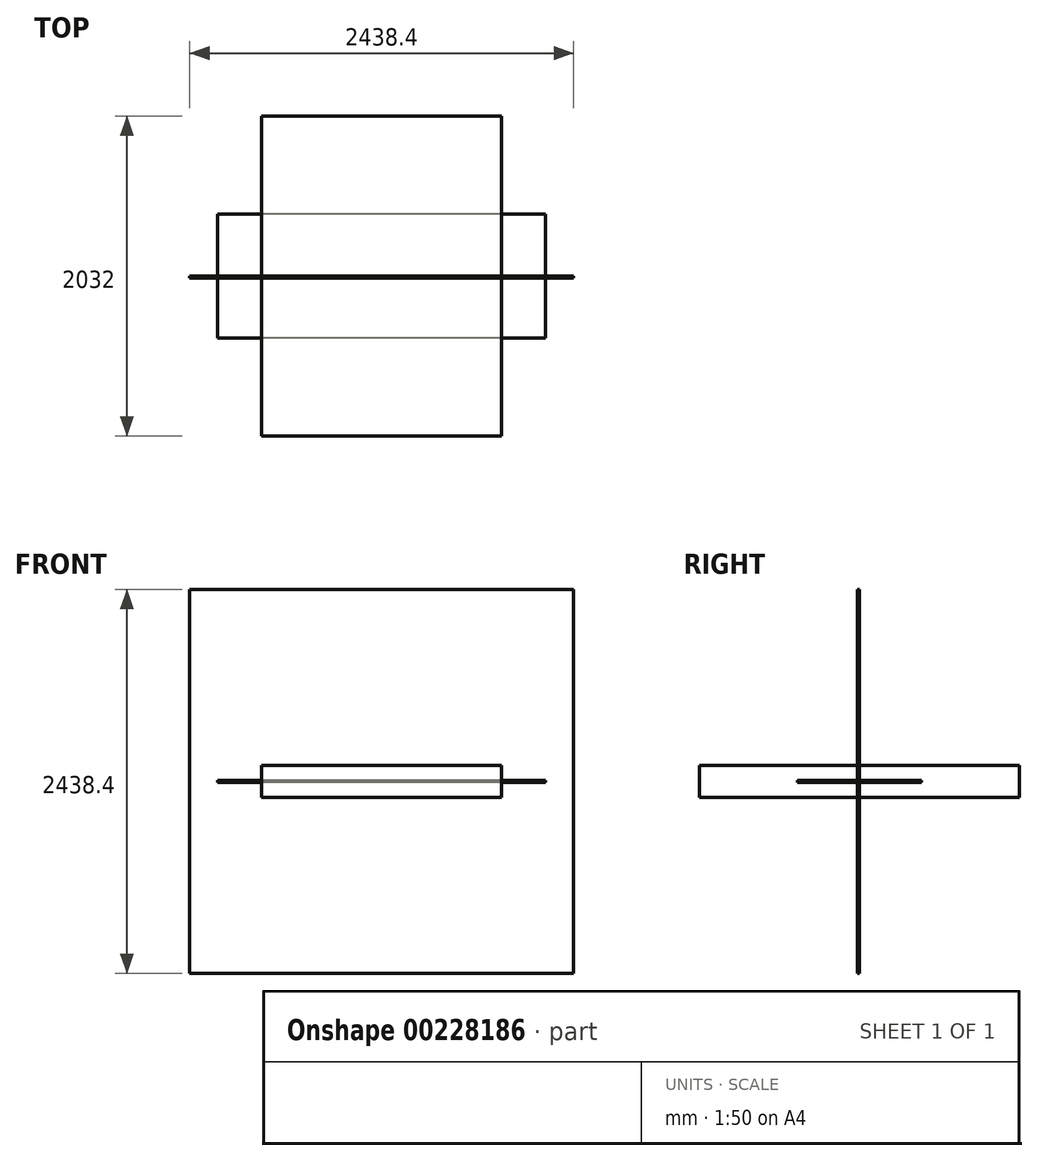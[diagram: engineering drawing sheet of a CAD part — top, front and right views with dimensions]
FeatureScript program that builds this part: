
annotation { "Feature Type Name" : "Feature", "Feature Type Description" : "" }
export const myFeature = defineFeature(function(context is Context, id is Id, definition is map)
    precondition{}
    {
        {
            var Q0;
            Q0=qCreatedBy(makeId("Top.planeOp"),FACE);
            var sketch = newSketch(context, id + "F0", { "sketchPlane" : qUnion([Q0])});
            skLineSegment(sketch, "E0.bottom", {"start": v(1041.4, 393.7) * mm, "end": v(-1041.4, 393.7) * mm});
            skLineSegment(sketch, "E0.top", {"start": v(1041.4, -393.7) * mm, "end": v(-1041.4, -393.7) * mm});
            skLineSegment(sketch, "E0.left", {"start": v(1041.4, 393.7) * mm, "end": v(1041.4, -393.7) * mm});
            skLineSegment(sketch, "E0.right", {"start": v(-1041.4, 393.7) * mm, "end": v(-1041.4, -393.7) * mm});
            skPoint(sketch, "E0.middle", {"position": v(0, 0) * mm});
            skSolve(sketch);
        }
        {
            var Q0;
            Q0=makeQuery(id+"F0.imprint","IMPRINT",FACE,{"disambiguationData":[TD([[makeQuery(id+"F0.imprint","IMPRINT",EDGE,{"derivedFrom":sQuery(id+"F0.wireOp",EDGE,"E0.bottom")}),1.0]])]});
            extrude(context, id + "F1", {"entities" : qUnion([Q0]), "endBound" : BoundingType.SYMMETRIC, "depth" : 11.9 * mm});
        }
        {
            var Q0;
            Q0=qCreatedBy(makeId("Top.planeOp"),FACE);
            var sketch = newSketch(context, id + "F2", { "sketchPlane" : qUnion([Q0])});
            skLineSegment(sketch, "E1.bottom", {"start": v(-762, 1016) * mm, "end": v(762, 1016) * mm});
            skLineSegment(sketch, "E1.top", {"start": v(-762, -1016) * mm, "end": v(762, -1016) * mm});
            skLineSegment(sketch, "E1.left", {"start": v(-762, 1016) * mm, "end": v(-762, -1016) * mm});
            skLineSegment(sketch, "E1.right", {"start": v(762, 1016) * mm, "end": v(762, -1016) * mm});
            skPoint(sketch, "E1.middle", {"position": v(0, 0) * mm});
            skSolve(sketch);
        }
        {
            var Q0;
            Q0 = qSketchRegion(id + "F2", true);
            extrude(context, id + "F3", {"entities" : qUnion([Q0]), "endBound" : BoundingType.SYMMETRIC, "depth" : 203.2 * mm});
        }
        {
            var Q0;
            Q0=qCreatedBy(makeId("Front.planeOp"),FACE);
            var sketch = newSketch(context, id + "F4", { "sketchPlane" : qUnion([Q0])});
            skLineSegment(sketch, "E2.bottom", {"start": v(1219.2, 1219.2) * mm, "end": v(-1219.2, 1219.2) * mm});
            skLineSegment(sketch, "E2.top", {"start": v(1219.2, -1219.2) * mm, "end": v(-1219.2, -1219.2) * mm});
            skLineSegment(sketch, "E2.left", {"start": v(1219.2, 1219.2) * mm, "end": v(1219.2, -1219.2) * mm});
            skLineSegment(sketch, "E2.right", {"start": v(-1219.2, 1219.2) * mm, "end": v(-1219.2, -1219.2) * mm});
            skPoint(sketch, "E2.middle", {"position": v(0, 0) * mm});
            skSolve(sketch);
        }
        {
            var Q0;
            Q0 = qSketchRegion(id + "F4", true);
            extrude(context, id + "F5", {"entities" : qUnion([Q0]), "depth" : 12.7 * mm});
        }
    });
